# Revit family: NLRS_27_GM_LIB_GIP_MR
name_source: partatom
category: Generic Models
revit_build: Autodesk Revit 2017 (Build: 20190507_1515(x64)
units: mm (PartAtom-declared; Revit-internal decimal feet)

## family parameters
Can host rebar = No
Cut with Voids When Loaded = Yes
Part Type = Normal
Room Calculation Point = No
Round Connector Dimension = Use Diameter
Shared = No

## types (6) — shared parameters
01_kraal = No
02_Trim = Yes
03_druppel = Yes
Assembly Code = 27.16
Description = GIP Goot
IfcExportAs = IfcFlowsegment
Manufacturer = Meilof Riks
Model = GIP
NLRS_C_Materiaal = RAL 9010 MR
Type Image = <None>
URL = https://www.meilofriks.nl
Vorm_Goot_L = 01 : 2_←_Hoek_L
Vorm_Goot_L-R = 01 : 4_↔_Hoek_L-R
Vorm_Goot_R = 01 : 3_→_Hoek_R
zero-valued in all types: Cost

## per-type parameters (varying)
| type | Breedte_Plafond | Breedte_goot | Breedte_goot_hoek | Diepte_bak | Hoogte_AK | Hoogte_VK | NLRS_C_Binnenbak | Set_Diepte_bak | set_Hoogte_AK |
| GIP280 | 250 mm  [stored 0.82021 ft] | 280 mm  [stored 0.918635 ft] | 280 mm  [stored 0.918635 ft] | 88 mm  [stored 0.288714 ft] | 215 mm | 186 mm  [stored 0.610236 ft] | RAL 9006 MR | 88 mm  [stored 0.288714 ft] | 215 mm |
| GIP230 | 200 mm  [stored 0.656168 ft] | 230 mm  [stored 0.754593 ft] | 230 mm  [stored 0.754593 ft] | 70 mm  [stored 0.229659 ft] | 225 mm  [stored 0.738189 ft] | 197 mm | RAL 9010 MR | 70 mm  [stored 0.229659 ft] | 225 mm  [stored 0.738189 ft] |
| GIP310 | 200 mm  [stored 0.656168 ft] | 310 mm  [stored 1.01706 ft] | 310 mm  [stored 1.01706 ft] | 74 mm  [stored 0.242782 ft] | 221 mm  [stored 0.725066 ft] | 197 mm | RAL 9010 MR | 74 mm  [stored 0.242782 ft] | 222 mm |
| GIP365 | 200 mm  [stored 0.656168 ft] | 365 mm  [stored 1.19751 ft] | 365 mm  [stored 1.19751 ft] | 95 mm | 248 mm  [stored 0.813648 ft] | 220 mm  [stored 0.721785 ft] | RAL 9010 MR | 95 mm | 248 mm  [stored 0.813648 ft] |
| GIP400 | 200 mm  [stored 0.656168 ft] | 400 mm  [stored 1.31234 ft] | 400 mm  [stored 1.31234 ft] | 78 mm  [stored 0.255906 ft] | 227 mm  [stored 0.744751 ft] | 201 mm  [stored 0.659449 ft] | RAL 9010 MR | 78 mm  [stored 0.255906 ft] | 227 mm  [stored 0.744751 ft] |
| GIP500 | 200 mm  [stored 0.656168 ft] | 500 mm  [stored 1.64042 ft] | 500 mm  [stored 1.64042 ft] | 79 mm | 227 mm  [stored 0.744751 ft] | 201 mm  [stored 0.659449 ft] | RAL 9010 MR | 79 mm | 227 mm  [stored 0.744751 ft] |

note: [stored X ft] marks values corroborated as IEEE doubles in the binary element streams (Revit-internal decimal feet)

## geometry (parser evidence)
native form markers: Sweep x33
no freeform markers — native parametric forms only
